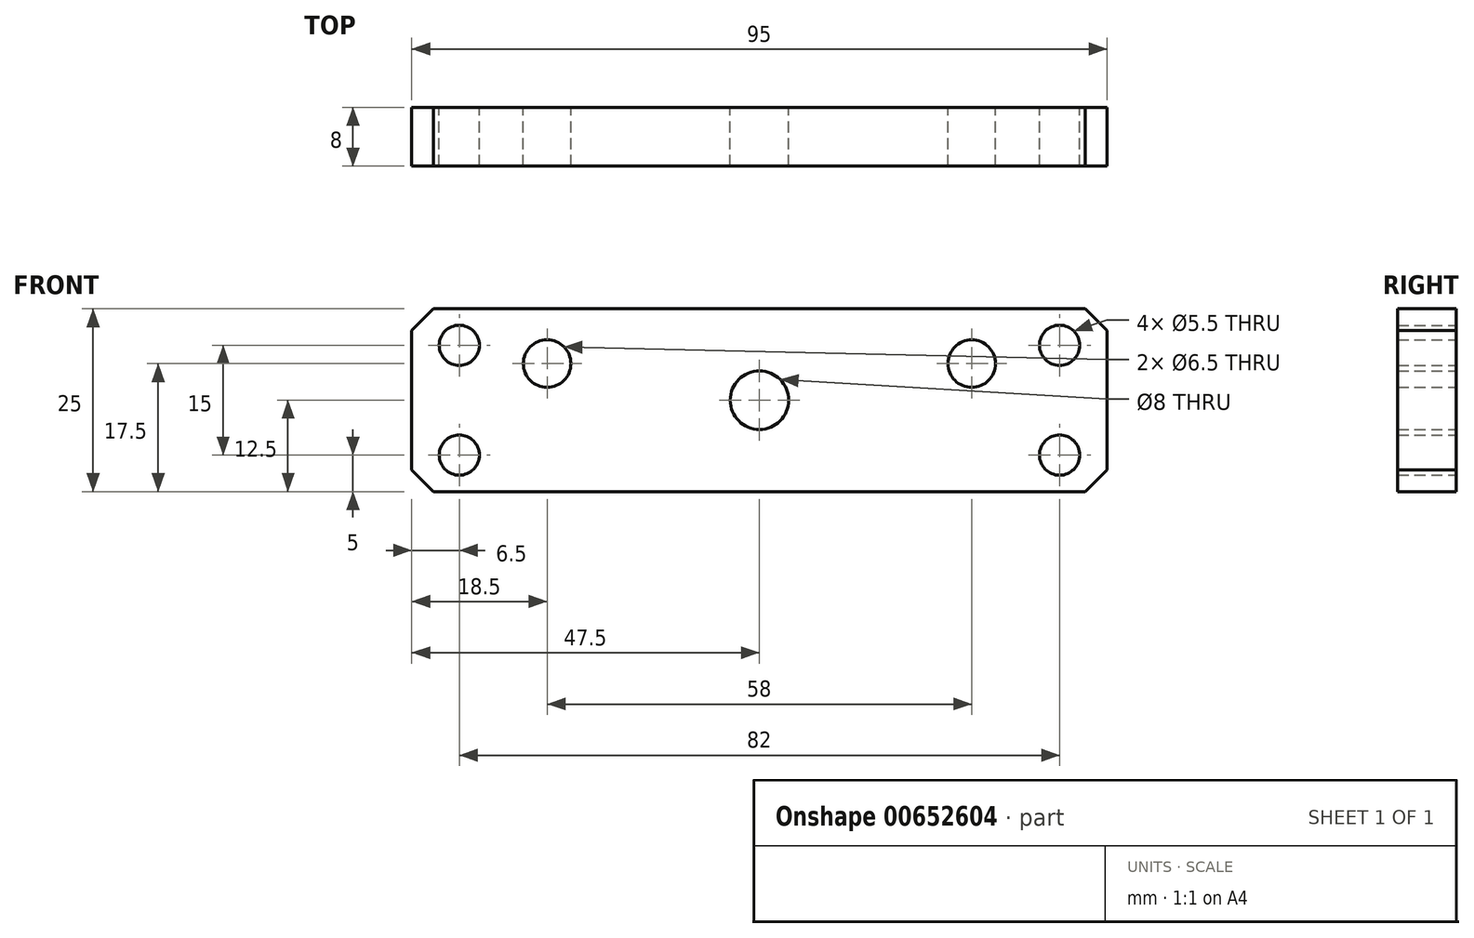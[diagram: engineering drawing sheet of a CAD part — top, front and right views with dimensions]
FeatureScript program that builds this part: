
annotation { "Feature Type Name" : "Feature", "Feature Type Description" : "" }
export const myFeature = defineFeature(function(context is Context, id is Id, definition is map)
    precondition{}
    {
        {
            var Q0;
            Q0=qCreatedBy(makeId("Front.planeOp"),FACE);
            var sketch = newSketch(context, id + "F0", { "sketchPlane" : qUnion([Q0])});
            skLineSegment(sketch, "E0.bottom", {"start": v(0, 0) * mm, "end": v(95, 0) * mm});
            skLineSegment(sketch, "E0.top", {"start": v(0, 25) * mm, "end": v(95, 25) * mm});
            skLineSegment(sketch, "E0.left", {"start": v(0, 0) * mm, "end": v(0, 25) * mm});
            skLineSegment(sketch, "E0.right", {"start": v(95, 0) * mm, "end": v(95, 25) * mm});
            skCircle(sketch, "E1", {"center": v(6.5, 20) * mm, "radius": 2.75 * mm});
            skCircle(sketch, "E2", {"center": v(6.5, 5) * mm, "radius": 2.75 * mm});
            skCircle(sketch, "E3", {"center": v(88.5, 5) * mm, "radius": 2.75 * mm});
            skCircle(sketch, "E4", {"center": v(88.5, 20) * mm, "radius": 2.75 * mm});
            skCircle(sketch, "E5", {"center": v(76.5, 17.5) * mm, "radius": 3.25 * mm});
            skCircle(sketch, "E6", {"center": v(18.5, 17.5) * mm, "radius": 3.25 * mm});
            skCircle(sketch, "E7", {"center": v(47.5, 12.5) * mm, "radius": 4 * mm});
            skSolve(sketch);
        }
        {
            var Q0;
            Q0=makeQuery(id+"F0.imprint","IMPRINT",FACE,{"disambiguationData":[TD([[makeQuery(id+"F0.imprint","IMPRINT",EDGE,{"derivedFrom":sQuery(id+"F0.wireOp",EDGE,"E0.bottom")}),1.0]])]});
            var Q1;
            Q1=makeQuery(id+"F0.imprint","IMPRINT",FACE,{"disambiguationData":[TD([[makeQuery(id+"F0.imprint","IMPRINT",EDGE,{"derivedFrom":sQuery(id+"F0.wireOp",EDGE,"E7")}),1.0]])]});
            extrude(context, id + "F1", {"entities" : qUnion([Q0, Q1]), "depth" : 8 * mm, "offsetDistance" : 25 * mm});
        }
        {
            var Q0;
            Q0=sQuery(id+"F0.wireOp",VERTEX,"E7.center");
            var Q1;
            Q1=makeQuery(id+"F1.opExtrude","SWEPT_BODY",BODY,{"disambiguationData":[OSD([sQuery(id+"F0.wireOp",EDGE,"E0.bottom"),sQuery(id+"F0.wireOp",EDGE,"E0.top"),sQuery(id+"F0.wireOp",EDGE,"E0.left"),sQuery(id+"F0.wireOp",EDGE,"E0.right")])]});
            hole(context, id + "F2", {"style" : HoleStyle.SIMPLE, "endStyle" : HoleEndStyle.THROUGH, "oppositeDirection" : true, "holeDiameter" : 8 * mm, "majorDiameter" : 5 * mm, "isTappedThrough" : true, "tappedDepth" : 12 * mm, "tapClearance" : 3, "locations" : qUnion([Q0]), "scope" : qUnion([Q1])});
        }
        {
            var Q0;
            Q0=makeQuery(id+"F1.opExtrude","SWEPT_EDGE",EDGE,{"disambiguationData":[OSD([sQuery(id+"F0.wireOp",EDGE,"E0.top"),sQuery(id+"F0.wireOp",EDGE,"E0.right")])]});
            var Q1;
            Q1=makeQuery(id+"F1.opExtrude","SWEPT_EDGE",EDGE,{"disambiguationData":[OSD([sQuery(id+"F0.wireOp",EDGE,"E0.bottom"),sQuery(id+"F0.wireOp",EDGE,"E0.right")])]});
            var Q2;
            Q2=makeQuery(id+"F1.opExtrude","SWEPT_EDGE",EDGE,{"disambiguationData":[OSD([sQuery(id+"F0.wireOp",EDGE,"E0.top"),sQuery(id+"F0.wireOp",EDGE,"E0.left")])]});
            var Q3;
            Q3=makeQuery(id+"F1.opExtrude","SWEPT_EDGE",EDGE,{"disambiguationData":[OSD([sQuery(id+"F0.wireOp",EDGE,"E0.bottom"),sQuery(id+"F0.wireOp",EDGE,"E0.left")])]});
            chamfer(context, id + "F3", {"entities" : qUnion([Q0, Q1, Q2, Q3]), "width" : 3 * mm, "tangentPropagation" : true});
        }
    });
